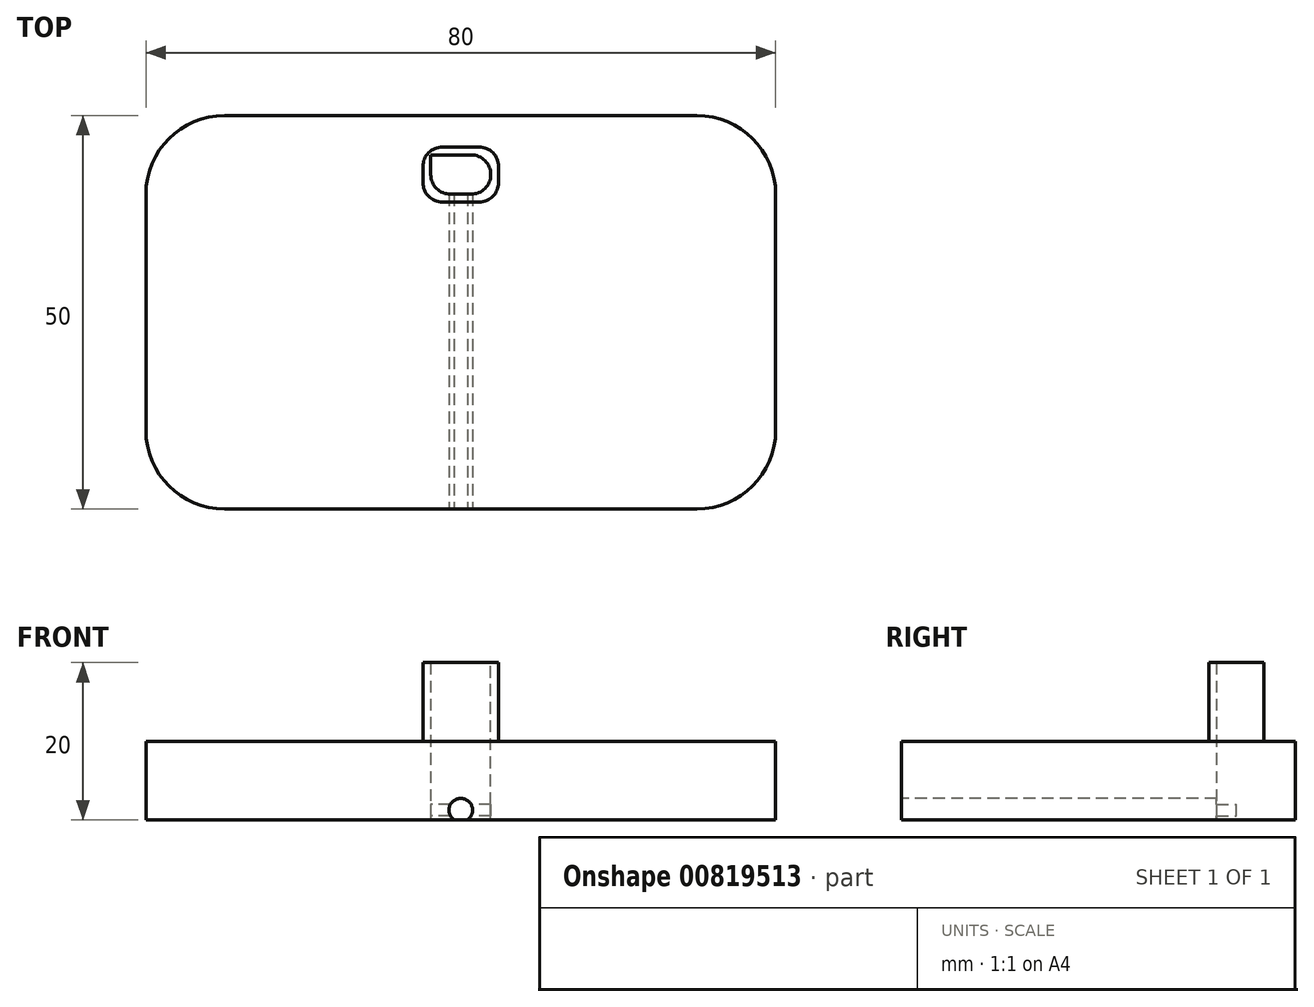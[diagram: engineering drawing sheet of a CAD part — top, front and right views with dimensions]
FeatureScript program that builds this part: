
annotation { "Feature Type Name" : "Feature", "Feature Type Description" : "" }
export const myFeature = defineFeature(function(context is Context, id is Id, definition is map)
    precondition{}
    {
        {
            var Q0;
            Q0=qCreatedBy(makeId("Top.planeOp"),FACE);
            var sketch = newSketch(context, id + "F0", { "sketchPlane" : qUnion([Q0])});
            skLineSegment(sketch, "E0.bottom", {"start": v(10, 0) * mm, "end": v(70, 0) * mm});
            skLineSegment(sketch, "E0.top", {"start": v(10, -50) * mm, "end": v(70, -50) * mm});
            skLineSegment(sketch, "E0.left", {"start": v(0, -10) * mm, "end": v(0, -40) * mm});
            skLineSegment(sketch, "E0.right", {"start": v(80, -10) * mm, "end": v(80, -40) * mm});
            skPoint(sketch, "E1.visualSharp", {"position": v(0, 0) * mm});
            skArc(sketch, "E1.filletArc", {"start": v(10, 0) * mm, "mid": v(2.93, -2.93) * mm, "end": v(0, -10) * mm});
            skPoint(sketch, "E2.visualSharp", {"position": v(80, 0) * mm});
            skArc(sketch, "E2.filletArc", {"start": v(80, -10) * mm, "mid": v(77.07, -2.93) * mm, "end": v(70, 0) * mm});
            skPoint(sketch, "E3.visualSharp", {"position": v(80, -50) * mm});
            skArc(sketch, "E3.filletArc", {"start": v(70, -50) * mm, "mid": v(77.07, -47.07) * mm, "end": v(80, -40) * mm});
            skPoint(sketch, "E4.visualSharp", {"position": v(0, -50) * mm});
            skArc(sketch, "E4.filletArc", {"start": v(0, -40) * mm, "mid": v(2.93, -47.07) * mm, "end": v(10, -50) * mm});
            skSolve(sketch);
        }
        {
            var Q0;
            Q0=makeQuery(id+"F0.imprint","IMPRINT",FACE,{"disambiguationData":[TD([[makeQuery(id+"F0.imprint","IMPRINT",EDGE,{"derivedFrom":sQuery(id+"F0.wireOp",EDGE,"E0.bottom")}),-1.0]])]});
            extrude(context, id + "F1", {"entities" : qUnion([Q0]), "depth" : 10 * mm, "offsetDistance" : 25 * mm});
        }
        {
            var Q0;
            Q0=makeQuery(id+"F1.opExtrude","SWEPT_FACE",FACE,{"disambiguationData":[OSD([sQuery(id+"F0.wireOp",EDGE,"E0.top")])]});
            var sketch = newSketch(context, id + "F2", { "sketchPlane" : qUnion([Q0])});
            skCircle(sketch, "E5", {"center": v(40, 1.25) * mm, "radius": 1.5 * mm});
            skPoint(sketch, "E5.centerSnap0", {"position": v(40, 0) * mm});
            skSolve(sketch);
        }
        {
            var Q0;
            {var subQ0=sQuery(id+"F2.wireOp",EDGE,"E5");var subQ1=makeQuery(id+"F1.opExtrude","CAP_EDGE",EDGE,{"disambiguationData":[OSD([sQuery(id+"F0.wireOp",EDGE,"E0.top")])],"isStart":true});var subQ2=makeQuery(id+"F2.imprint","INTERSECT",VERTEX,{"disambiguationData":[OD(0.0)],"derivedFrom":[subQ1,subQ0]});Q0=makeQuery(id+"F2.imprint","IMPRINT",FACE,{"disambiguationData":[TD([[makeQuery(id+"F2.imprint","IMPRINT",EDGE,{"disambiguationData":[TD([[subQ2,1.0]])],"derivedFrom":subQ0}),1.0]])]});}
            extrude(context, id + "F3", {"entities" : qUnion([Q0]), "operationType" : NewBodyOperationType.REMOVE, "oppositeDirection" : true, "depth" : 45 * mm, "offsetDistance" : 25 * mm});
        }
        {
            var Q0;
            Q0=makeQuery(id+"F1.opExtrude","CAP_FACE",FACE,{"disambiguationData":[OSD([sQuery(id+"F0.wireOp",EDGE,"E0.bottom"),sQuery(id+"F0.wireOp",EDGE,"E0.top"),sQuery(id+"F0.wireOp",EDGE,"E0.left"),sQuery(id+"F0.wireOp",EDGE,"E0.right"),sQuery(id+"F0.wireOp",EDGE,"E1.filletArc"),sQuery(id+"F0.wireOp",EDGE,"E2.filletArc"),sQuery(id+"F0.wireOp",EDGE,"E3.filletArc"),sQuery(id+"F0.wireOp",EDGE,"E4.filletArc")])],"isStart":true});
            var sketch = newSketch(context, id + "F4", { "sketchPlane" : qUnion([Q0])});
            skPoint(sketch, "E6", {"position": v(39.17, 5) * mm});
            skPoint(sketch, "E7", {"position": v(40.83, 5) * mm});
            skLineSegment(sketch, "E8", {"start": v(39.17, 5) * mm, "end": v(36.19, 5) * mm});
            skLineSegment(sketch, "E9", {"start": v(40.83, 5) * mm, "end": v(43.81, 5) * mm});
            skLineSegment(sketch, "E10", {"start": v(36.19, 5) * mm, "end": v(36.19, 10) * mm});
            skLineSegment(sketch, "E11", {"start": v(36.19, 10) * mm, "end": v(43.81, 10) * mm});
            skLineSegment(sketch, "E12", {"start": v(43.81, 10) * mm, "end": v(43.81, 5) * mm});
            skLineSegment(sketch, "E13.top", {"start": v(36.19, 5) * mm, "end": v(43.81, 5) * mm});
            skLineSegment(sketch, "E13.left", {"start": v(36.19, 10) * mm, "end": v(36.19, 5) * mm});
            skSolve(sketch);
        }
        {
            var Q0;
            {var subQ0=sQuery(id+"F4.wireOp",EDGE,"E13.left");Q0=makeQuery(id+"F4.imprint","IMPRINT",FACE,{"disambiguationData":[TD([[makeQuery(id+"F4.imprint","IMPRINT",EDGE,{"derivedFrom":subQ0}),1.0]])]});}
            var Q1;
            {var subQ0=sQuery(id+"F4.wireOp",EDGE,"E11");var subQ1=sQuery(id+"F2.wireOp",EDGE,"E5");var subQ2=sQuery(id+"F0.wireOp",EDGE,"E0.top");var subQ3=makeQuery(id+"F1.opExtrude","CAP_EDGE",EDGE,{"disambiguationData":[OSD([subQ2])],"isStart":true});var subQ4=makeQuery(id+"F3.boolean.opBoolean","COPY",EDGE,{"derivedFrom":makeQuery(id+"F3.opExtrude","SWEPT_EDGE",EDGE,{"disambiguationData":[OSD([subQ2,subQ1]),TDD([makeQuery(id+"F2.imprint","INTERSECT",VERTEX,{"disambiguationData":[OD(0.0)],"derivedFrom":[subQ3,subQ1]})])]})});var subQ5=makeQuery(id+"F4.imprint","INTERSECT",VERTEX,{"derivedFrom":[subQ4,subQ0]});Q1=makeQuery(id+"F4.imprint","IMPRINT",FACE,{"disambiguationData":[TD([[makeQuery(id+"F4.imprint","IMPRINT",EDGE,{"disambiguationData":[TD([[subQ5,-1.0]])],"derivedFrom":subQ0}),-1.0]])]});}
            var Q2;
            {var subQ0=sQuery(id+"F4.wireOp",EDGE,"E12");Q2=makeQuery(id+"F4.imprint","IMPRINT",FACE,{"disambiguationData":[TD([[makeQuery(id+"F4.imprint","IMPRINT",EDGE,{"derivedFrom":subQ0}),-1.0]])]});}
            extrude(context, id + "F5", {"entities" : qUnion([Q0, Q1, Q2]), "operationType" : NewBodyOperationType.REMOVE, "oppositeDirection" : true, "depth" : 25 * mm, "offsetDistance" : 25 * mm});
        }
        {
            var Q0;
            Q0=makeQuery(id+"F5.boolean.opBoolean","COPY",EDGE,{"derivedFrom":makeQuery(id+"F5.opExtrude","SWEPT_EDGE",EDGE,{"disambiguationData":[OSD([sQuery(id+"F4.wireOp",EDGE,"E13.top"),sQuery(id+"F4.wireOp",EDGE,"E13.left")])]})});
            var Q1;
            Q1=makeQuery(id+"F5.boolean.opBoolean","COPY",EDGE,{"derivedFrom":makeQuery(id+"F5.opExtrude","SWEPT_EDGE",EDGE,{"disambiguationData":[OSD([sQuery(id+"F4.wireOp",EDGE,"E13.top"),sQuery(id+"F4.wireOp",EDGE,"E12")])]})});
            var Q2;
            Q2=makeQuery(id+"F5.boolean.opBoolean","COPY",EDGE,{"derivedFrom":makeQuery(id+"F5.opExtrude","SWEPT_EDGE",EDGE,{"disambiguationData":[OSD([sQuery(id+"F4.wireOp",EDGE,"E11"),sQuery(id+"F4.wireOp",EDGE,"E12")])]})});
            var Q3;
            Q3=makeQuery(id+"F5.boolean.opBoolean","COPY",EDGE,{"derivedFrom":makeQuery(id+"F5.opExtrude","SWEPT_EDGE",EDGE,{"disambiguationData":[OSD([sQuery(id+"F4.wireOp",EDGE,"E11"),sQuery(id+"F4.wireOp",EDGE,"E13.left")])]})});
            fillet(context, id + "F6", {"entities" : qUnion([Q0, Q1, Q2, Q3]), "radius" : 2.5 * mm, "tangentPropagation" : true, "allowEdgeOverflow" : false});
        }
        {
            var Q0;
            Q0=makeQuery(id+"F1.opExtrude","CAP_FACE",FACE,{"disambiguationData":[OSD([sQuery(id+"F0.wireOp",EDGE,"E0.bottom"),sQuery(id+"F0.wireOp",EDGE,"E0.top"),sQuery(id+"F0.wireOp",EDGE,"E0.left"),sQuery(id+"F0.wireOp",EDGE,"E0.right"),sQuery(id+"F0.wireOp",EDGE,"E1.filletArc"),sQuery(id+"F0.wireOp",EDGE,"E2.filletArc"),sQuery(id+"F0.wireOp",EDGE,"E3.filletArc"),sQuery(id+"F0.wireOp",EDGE,"E4.filletArc")])],"isStart":false});
            var sketch = newSketch(context, id + "F7", { "sketchPlane" : qUnion([Q0])});
            skPoint(sketch, "E14", {"position": v(40, -10) * mm});
            skPoint(sketch, "E15", {"position": v(40, -5) * mm});
            skPoint(sketch, "E16", {"position": v(36.19, -7.5) * mm});
            skPoint(sketch, "E17", {"position": v(43.81, -7.5) * mm});
            skPoint(sketch, "E18", {"position": v(40, -11) * mm});
            skPoint(sketch, "E19", {"position": v(44.81, -7.5) * mm});
            skPoint(sketch, "E20", {"position": v(40, -4) * mm});
            skPoint(sketch, "E21", {"position": v(35.19, -7.5) * mm});
            skLineSegment(sketch, "E22", {"start": v(40, -11) * mm, "end": v(44.81, -11) * mm});
            skLineSegment(sketch, "E23", {"start": v(44.81, -11) * mm, "end": v(44.81, -4) * mm});
            skLineSegment(sketch, "E24", {"start": v(44.81, -4) * mm, "end": v(35.19, -4) * mm});
            skLineSegment(sketch, "E25", {"start": v(35.19, -4) * mm, "end": v(35.19, -11) * mm});
            skLineSegment(sketch, "E26", {"start": v(35.19, -11) * mm, "end": v(40, -11) * mm});
            skSolve(sketch);
        }
        {
            var Q0;
            Q0=makeQuery(id+"F7.imprint","IMPRINT",FACE,{"disambiguationData":[TD([[makeQuery(id+"F7.imprint","IMPRINT",EDGE,{"derivedFrom":sQuery(id+"F7.wireOp",EDGE,"E22")}),1.0]])]});
            extrude(context, id + "F8", {"entities" : qUnion([Q0]), "operationType" : NewBodyOperationType.ADD, "depth" : 10 * mm, "offsetDistance" : 25 * mm});
        }
        {
            var Q0;
            Q0=makeQuery(id+"F8.opExtrude","SWEPT_EDGE",EDGE,{"disambiguationData":[OSD([sQuery(id+"F7.wireOp",EDGE,"E23"),sQuery(id+"F7.wireOp",EDGE,"E24")])]});
            var Q1;
            Q1=makeQuery(id+"F8.opExtrude","SWEPT_EDGE",EDGE,{"disambiguationData":[OSD([sQuery(id+"F7.wireOp",EDGE,"E24"),sQuery(id+"F7.wireOp",EDGE,"E25")])]});
            var Q2;
            Q2=makeQuery(id+"F8.opExtrude","SWEPT_EDGE",EDGE,{"disambiguationData":[OSD([sQuery(id+"F7.wireOp",EDGE,"E25"),sQuery(id+"F7.wireOp",EDGE,"E26")])]});
            var Q3;
            Q3=makeQuery(id+"F8.opExtrude","SWEPT_EDGE",EDGE,{"disambiguationData":[OSD([sQuery(id+"F7.wireOp",EDGE,"E22"),sQuery(id+"F7.wireOp",EDGE,"E23")])]});
            fillet(context, id + "F9", {"entities" : qUnion([Q0, Q1, Q2, Q3]), "radius" : 2.5 * mm, "tangentPropagation" : true, "allowEdgeOverflow" : false});
        }
    });
